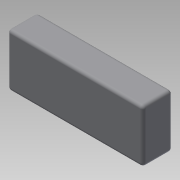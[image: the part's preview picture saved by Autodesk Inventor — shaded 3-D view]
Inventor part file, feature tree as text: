
AUTODESK INVENTOR PART (.ipt)
format: ipt  version: 2015 SP1 (Build 190203100, 203)  size: 94,208 bytes
history: native  units: mm
features: sketch x2, extrude x1, fillet x1
ambient origin geometry x8: Origin, YZ Plane, XZ Plane, XY Plane, X Axis, Y Axis, Z Axis, Center Point
bodies: Solid1 (feature_tree)
feature tree (4):
  extrude  "Extrusion1"  Depth=34.0mm
  fillet  "Fillet1"  Radius=19.0mm
  sketch  "Sketch2"  dims[d4=2.0mm d5=2.0mm d6=2.0mm]
  sketch  "Sketch1"  dims[d0=87.0mm d1=34.0mm d2=19.0mm d3=0.0mm]
